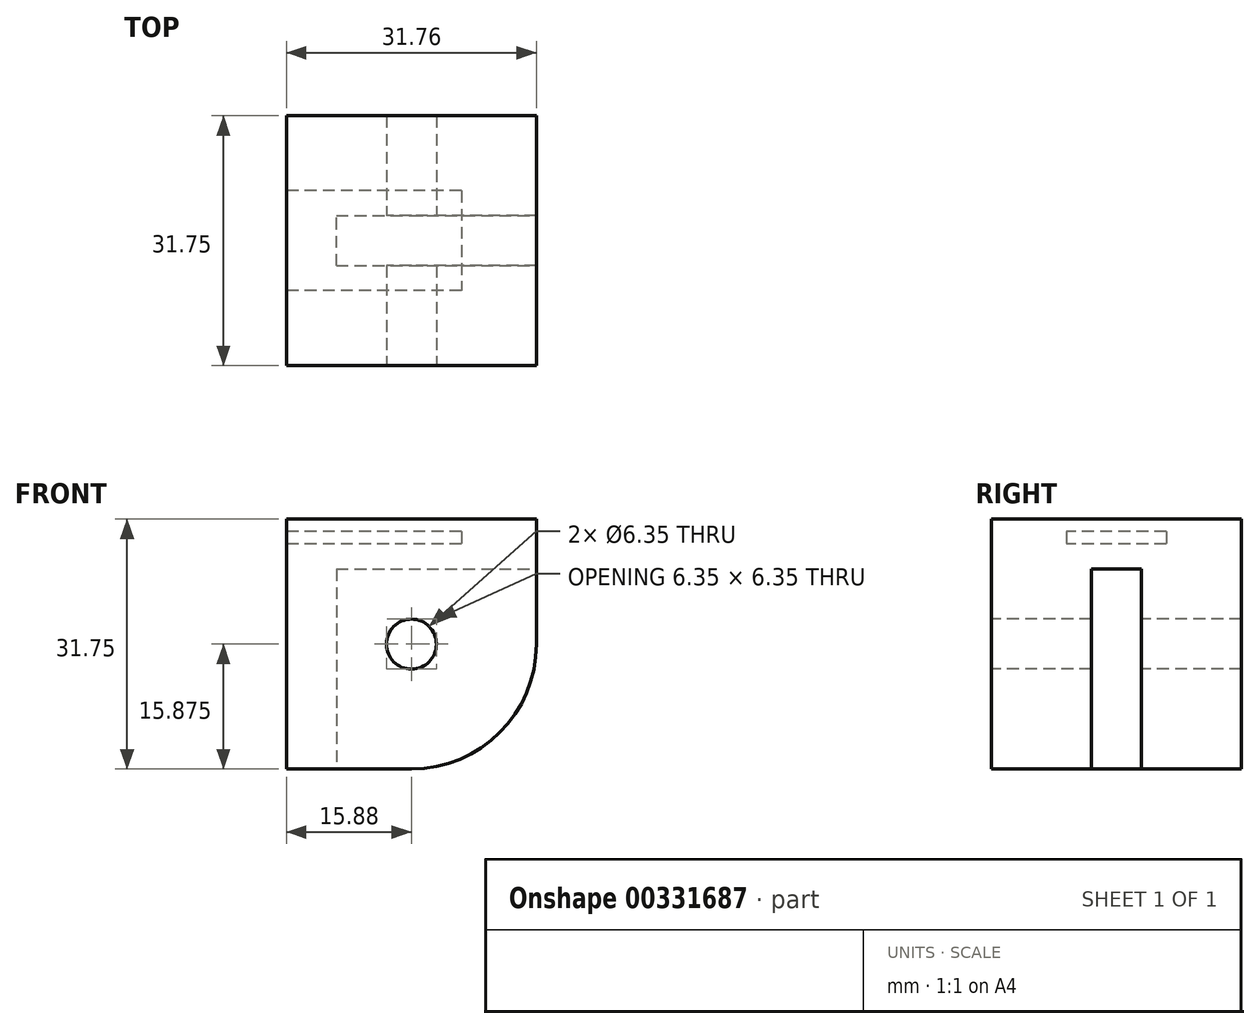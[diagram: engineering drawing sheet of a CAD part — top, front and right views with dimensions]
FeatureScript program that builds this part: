
annotation { "Feature Type Name" : "Feature", "Feature Type Description" : "" }
export const myFeature = defineFeature(function(context is Context, id is Id, definition is map)
    precondition{}
    {
        {
            var Q0;
            Q0=qCreatedBy(makeId("Front.planeOp"),FACE);
            var sketch = newSketch(context, id + "F0", { "sketchPlane" : qUnion([Q0])});
            skLineSegment(sketch, "E0", {"start": v(15.88, 0) * mm, "end": v(-15.88, 0) * mm});
            skLineSegment(sketch, "E1", {"start": v(-15.88, 0) * mm, "end": v(-15.87, -31.75) * mm});
            skLineSegment(sketch, "E2", {"start": v(-15.88, -31.75) * mm, "end": v(0, -31.75) * mm});
            skLineSegment(sketch, "E3", {"start": v(15.88, 0) * mm, "end": v(15.88, -15.88) * mm});
            skArc(sketch, "E4", {"start": v(0, -31.75) * mm, "mid": v(11.23, -27.1) * mm, "end": v(15.88, -15.88) * mm});
            skLineSegment(sketch, "E5.bottom", {"start": v(0, -15.88) * mm, "end": v(0, -15.88) * mm});
            skLineSegment(sketch, "E5.top", {"start": v(0, -15.88) * mm, "end": v(0, -15.88) * mm});
            skLineSegment(sketch, "E5.left", {"start": v(0, -15.88) * mm, "end": v(0, -15.88) * mm});
            skLineSegment(sketch, "E5.right", {"start": v(0, -15.88) * mm, "end": v(0, -15.88) * mm});
            skCircle(sketch, "E6", {"center": v(0, -15.88) * mm, "radius": 3.18 * mm});
            skSolve(sketch);
        }
        {
            var Q0;
            Q0 = qSketchRegion(id + "F0", true);
            extrude(context, id + "F1", {"entities" : qUnion([Q0]), "oppositeDirection" : true, "depth" : 31.75 * mm});
        }
        {
            var Q0;
            Q0=makeQuery(id+"F1.opExtrude","SWEPT_FACE",FACE,{"disambiguationData":[OSD([sQuery(id+"F0.wireOp",EDGE,"E2")])]});
            var sketch = newSketch(context, id + "F2", { "sketchPlane" : qUnion([Q0])});
            skLineSegment(sketch, "E7.bottom", {"start": v(-9.53, -12.7) * mm, "end": v(15.88, -12.7) * mm});
            skLineSegment(sketch, "E7.top", {"start": v(-9.53, -19.05) * mm, "end": v(15.88, -19.05) * mm});
            skLineSegment(sketch, "E7.left", {"start": v(-9.53, -12.7) * mm, "end": v(-9.53, -19.05) * mm});
            skLineSegment(sketch, "E7.right", {"start": v(15.88, -12.7) * mm, "end": v(15.88, -19.05) * mm});
            skSolve(sketch);
        }
        {
            var Q0;
            {var subQ0=sQuery(id+"F2.wireOp",EDGE,"E7.right");Q0=makeQuery(id+"F2.imprint","IMPRINT",FACE,{"disambiguationData":[TD([[makeQuery(id+"F2.imprint","IMPRINT",EDGE,{"derivedFrom":subQ0}),-1.0]])]});}
            var Q1;
            {var subQ0=sQuery(id+"F2.wireOp",EDGE,"E7.left");Q1=makeQuery(id+"F2.imprint","IMPRINT",FACE,{"disambiguationData":[TD([[makeQuery(id+"F2.imprint","IMPRINT",EDGE,{"derivedFrom":subQ0}),1.0]])]});}
            extrude(context, id + "F3", {"entities" : qUnion([Q0, Q1]), "operationType" : NewBodyOperationType.REMOVE, "oppositeDirection" : true, "depth" : 25.4 * mm});
        }
        {
            var Q0;
            Q0=makeQuery(id+"F1.opExtrude","SWEPT_FACE",FACE,{"disambiguationData":[OSD([sQuery(id+"F0.wireOp",EDGE,"E1")])]});
            var sketch = newSketch(context, id + "F4", { "sketchPlane" : qUnion([Q0])});
            skLineSegment(sketch, "E8.bottom", {"start": v(-22.23, -1.59) * mm, "end": v(-9.53, -1.59) * mm});
            skLineSegment(sketch, "E8.top", {"start": v(-22.23, -3.17) * mm, "end": v(-9.53, -3.17) * mm});
            skLineSegment(sketch, "E8.left", {"start": v(-22.23, -1.59) * mm, "end": v(-22.23, -3.17) * mm});
            skLineSegment(sketch, "E8.right", {"start": v(-9.53, -1.59) * mm, "end": v(-9.53, -3.17) * mm});
            skSolve(sketch);
        }
        {
            var Q0;
            Q0 = qSketchRegion(id + "F4", true);
            extrude(context, id + "F5", {"entities" : qUnion([Q0]), "operationType" : NewBodyOperationType.REMOVE, "oppositeDirection" : true, "depth" : 22.22 * mm});
        }
    });
